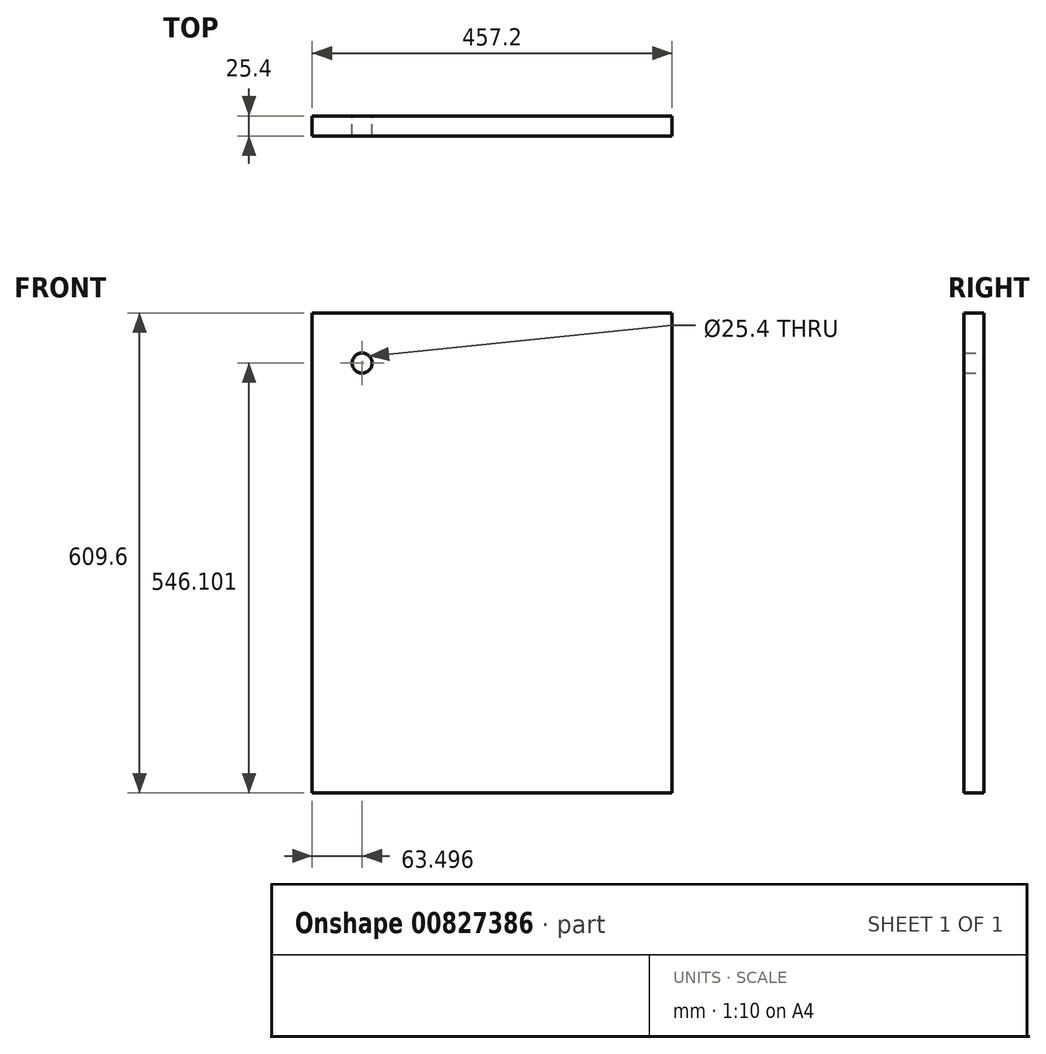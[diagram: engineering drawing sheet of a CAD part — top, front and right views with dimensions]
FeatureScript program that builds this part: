
annotation { "Feature Type Name" : "Feature", "Feature Type Description" : "" }
export const myFeature = defineFeature(function(context is Context, id is Id, definition is map)
    precondition{}
    {
        {
            var Q0;
            Q0=qCreatedBy(makeId("Front.planeOp"),FACE);
            var sketch = newSketch(context, id + "F0", { "sketchPlane" : qUnion([Q0])});
            skLineSegment(sketch, "E0.bottom", {"start": v(-410.8, 305.38) * mm, "end": v(46.4, 305.38) * mm});
            skLineSegment(sketch, "E0.top", {"start": v(-410.8, -304.22) * mm, "end": v(46.4, -304.22) * mm});
            skLineSegment(sketch, "E0.left", {"start": v(-410.8, 305.38) * mm, "end": v(-410.8, -304.22) * mm});
            skLineSegment(sketch, "E0.right", {"start": v(46.4, 305.38) * mm, "end": v(46.4, -304.22) * mm});
            skSolve(sketch);
        }
        {
            var Q0;
            Q0 = qSketchRegion(id + "F0", true);
            extrude(context, id + "F1", {"entities" : qUnion([Q0]), "depth" : 25.4 * mm, "offsetDistance" : 25.4 * mm});
        }
        {
            var Q0;
            Q0=qCreatedBy(makeId("Front.planeOp"),FACE);
            var sketch = newSketch(context, id + "F2", { "sketchPlane" : qUnion([Q0])});
            skCircle(sketch, "E1", {"center": v(-347.3, 241.88) * mm, "radius": 12.7 * mm});
            skCircle(sketch, "E2", {"center": v(-283.8, 241.88) * mm, "radius": 12.7 * mm});
            skSolve(sketch);
        }
        {
            var Q0;
            Q0=sQuery(id+"F2.wireOp",VERTEX,"E1.center");
            var Q1;
            Q1=makeQuery(id+"F1.opExtrude","SWEPT_BODY",BODY,{"disambiguationData":[OSD([sQuery(id+"F0.wireOp",EDGE,"E0.bottom"),sQuery(id+"F0.wireOp",EDGE,"E0.top"),sQuery(id+"F0.wireOp",EDGE,"E0.left"),sQuery(id+"F0.wireOp",EDGE,"E0.right")])]});
            hole(context, id + "F3", {"style" : HoleStyle.SIMPLE, "endStyle" : HoleEndStyle.THROUGH, "oppositeDirection" : true, "holeDiameter" : 25.4 * mm, "majorDiameter" : 6.35 * mm, "isTappedThrough" : true, "tappedDepth" : 12.7 * mm, "tapClearance" : 3, "locations" : qUnion([Q0]), "scope" : qUnion([Q1])});
        }
    });
